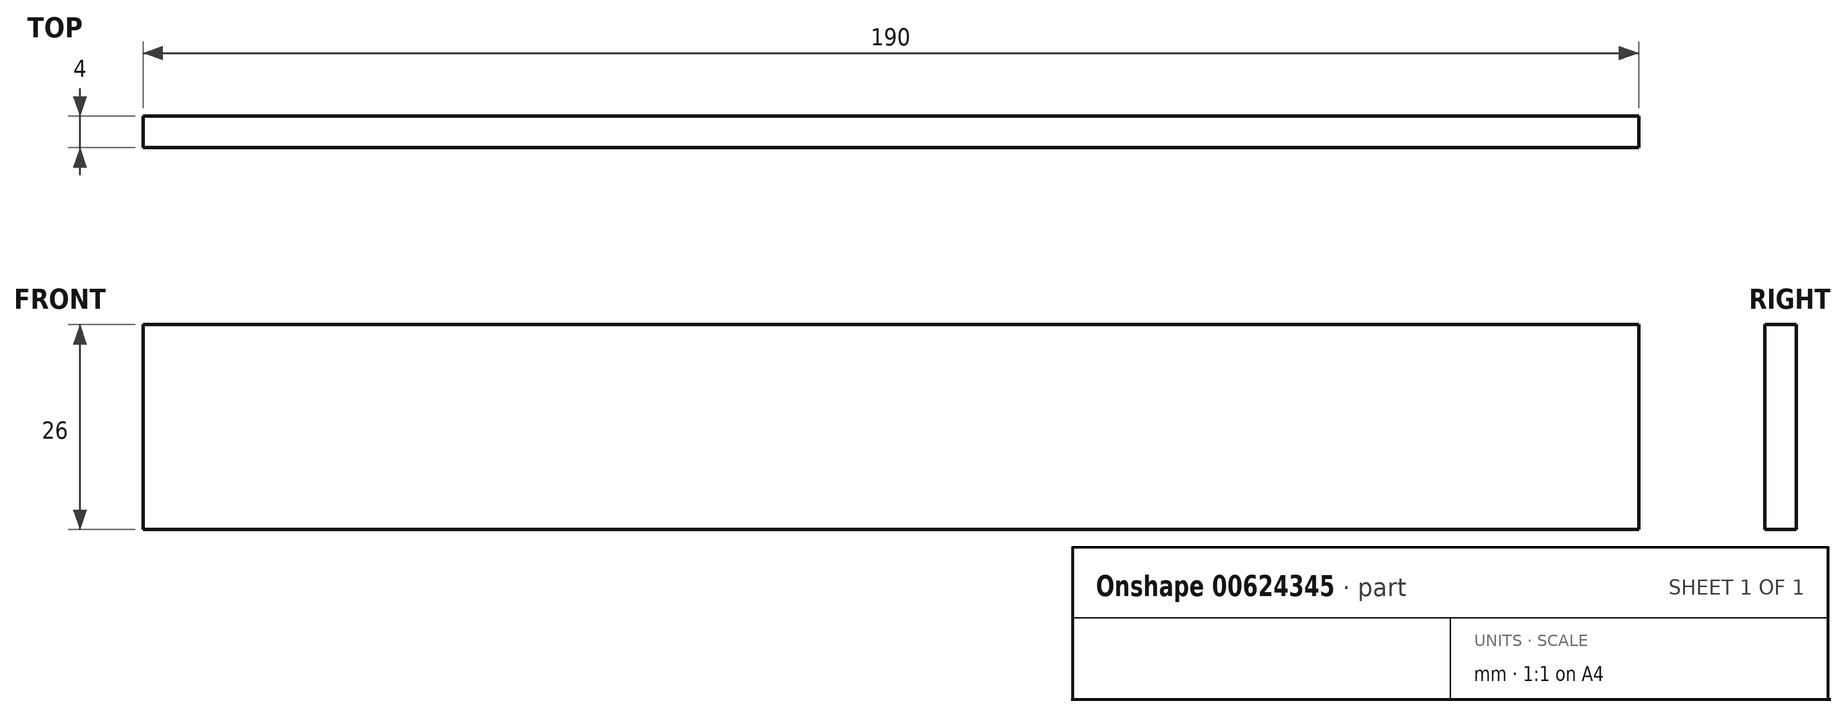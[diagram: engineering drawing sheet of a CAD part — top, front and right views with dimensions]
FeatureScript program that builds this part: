
annotation { "Feature Type Name" : "Feature", "Feature Type Description" : "" }
export const myFeature = defineFeature(function(context is Context, id is Id, definition is map)
    precondition{}
    {
        {
            var Q0;
            Q0=qCreatedBy(makeId("Front.planeOp"),FACE);
            var sketch = newSketch(context, id + "F0", { "sketchPlane" : qUnion([Q0])});
            skLineSegment(sketch, "E0.bottom", {"start": v(-95, 13) * mm, "end": v(95, 13) * mm});
            skLineSegment(sketch, "E0.top", {"start": v(-95, -13) * mm, "end": v(95, -13) * mm});
            skLineSegment(sketch, "E0.left", {"start": v(-95, 13) * mm, "end": v(-95, -13) * mm});
            skLineSegment(sketch, "E0.right", {"start": v(95, 13) * mm, "end": v(95, -13) * mm});
            skPoint(sketch, "E0.middle", {"position": v(0, 0) * mm});
            skSolve(sketch);
        }
        {
            var Q0;
            Q0 = qSketchRegion(id + "F0", true);
            extrude(context, id + "F1", {"entities" : qUnion([Q0]), "depth" : 4 * mm, "offsetDistance" : 25 * mm});
        }
    });
